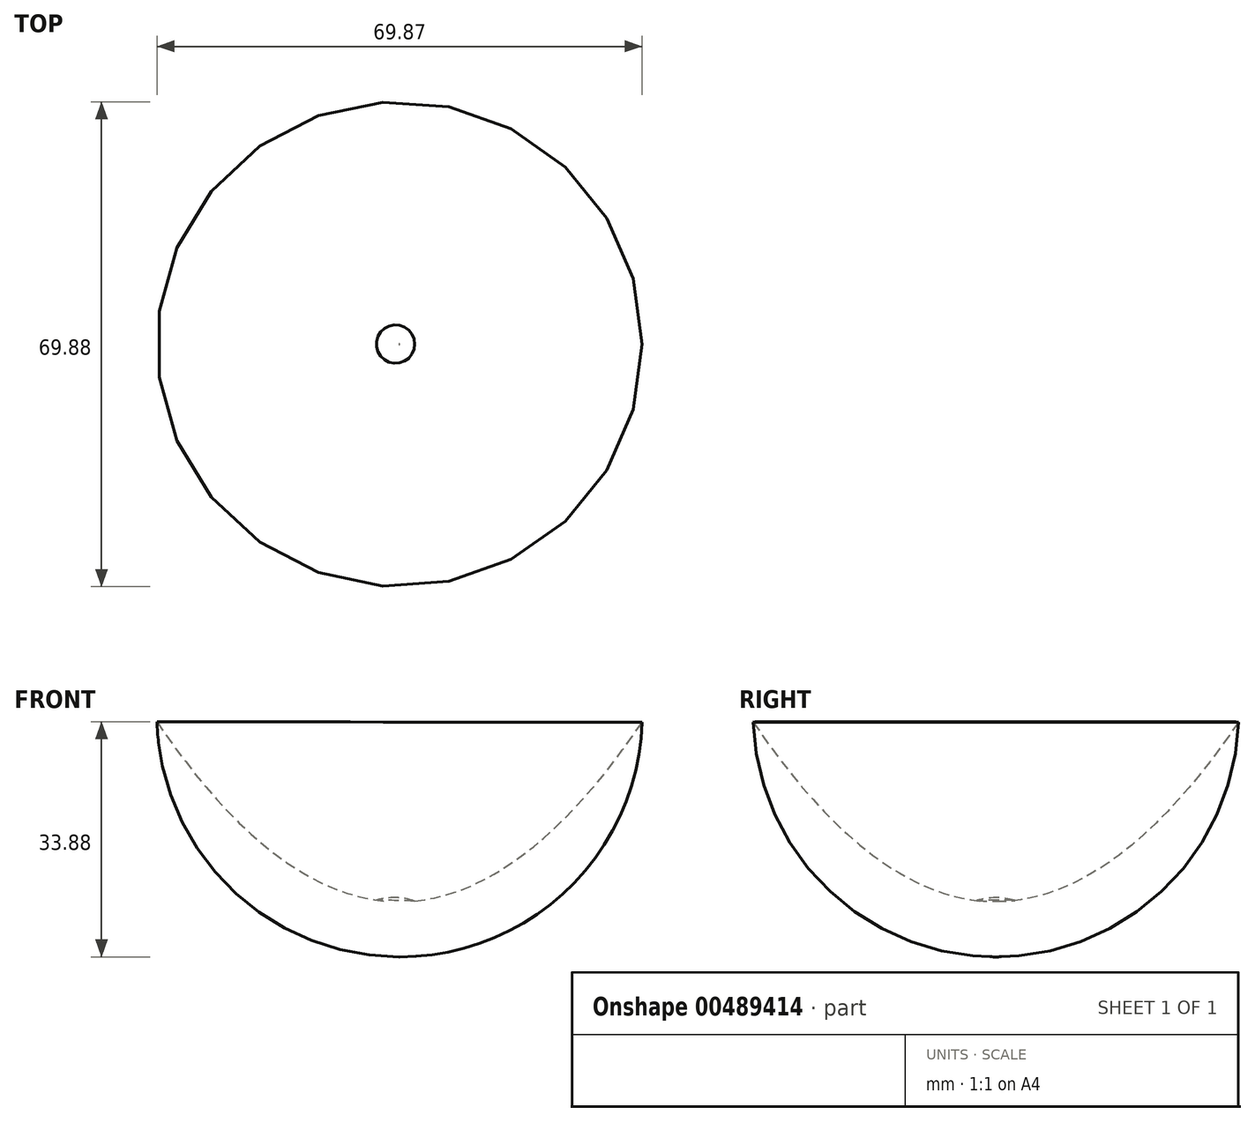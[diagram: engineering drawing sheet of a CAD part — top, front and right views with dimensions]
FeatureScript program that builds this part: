
annotation { "Feature Type Name" : "Feature", "Feature Type Description" : "" }
export const myFeature = defineFeature(function(context is Context, id is Id, definition is map)
    precondition{}
    {
        {
            var Q0;
            Q0=qCreatedBy(makeId("Front.planeOp"),FACE);
            var sketch = newSketch(context, id + "F0", { "sketchPlane" : qUnion([Q0])});
            skLineSegment(sketch, "E0", {"start": v(35.57, 70.99) * mm, "end": v(35.76, 70.99) * mm});
            skLineSegment(sketch, "E1", {"start": v(71.41, 35.92) * mm, "end": v(71.41, 35.79) * mm});
            skLineSegment(sketch, "E2", {"start": v(53.58, 0) * mm, "end": v(0, 0) * mm});
            skArc(sketch, "E3", {"start": v(70.67, 34.8) * mm, "mid": v(35.61, 70.84) * mm, "end": v(0.87, 34.5) * mm});
            skFitSpline(sketch, "E4", {"points": [v(-0.14, 35.5) * mm, v(35.7, 0) * mm, v(71.41, 35.92) * mm, v(70.69, 35.92) * mm], "startDerivative": vector(65.07, -127.42) * mm, "endDerivative": vector(-18.12, -6.85) * mm});
            skFitSpline(sketch, "E5", {"points": [v(56.44, 15.48) * mm, v(49.75, -23.32) * mm], "startDerivative": vector(-10.7, -38.8) * mm, "endDerivative": vector(-10.7, -38.8) * mm});
            skFitSpline(sketch, "E6.trimOffspring", {"points": [v(-0.14, 35.5) * mm, v(35.7, 0) * mm, v(71.41, 35.92) * mm, v(70.69, 35.92) * mm], "startDerivative": vector(65.07, -127.42) * mm, "endDerivative": vector(-18.12, -6.85) * mm});
            skLineSegment(sketch, "E7", {"start": v(35.76, 70.99) * mm, "end": v(35.7, 0) * mm});
            skPoint(sketch, "E7.startSnap0", {"position": v(35.57, 70.99) * mm});
            skFitSpline(sketch, "E8", {"points": [v(-0.14, 35.5) * mm, v(71.41, 35.92) * mm], "startDerivative": vector(71.86, -106.73) * mm, "endDerivative": vector(71.23, 107.5) * mm});
            skLineSegment(sketch, "E9", {"start": v(70.63, 33.99) * mm, "end": v(69.21, 32.6) * mm});
            skLineSegment(sketch, "E10", {"start": v(35.7, 0) * mm, "end": v(34.68, 1.01) * mm});
            skLineSegment(sketch, "E11", {"start": v(53.94, 17.75) * mm, "end": v(53.94, 17.75) * mm});
            skLineSegment(sketch, "E12.trimOffspring", {"start": v(0.87, 34.5) * mm, "end": v(-0.14, 35.5) * mm});
            skLineSegment(sketch, "E13.trimOffspring", {"start": v(36.74, 1) * mm, "end": v(35.7, 0) * mm});
            skArc(sketch, "E14.trimOffspring", {"start": v(0.9, 34) * mm, "mid": v(35.76, 1) * mm, "end": v(70.63, 33.99) * mm});
            skLineSegment(sketch, "E15", {"start": v(36.74, 1) * mm, "end": v(36.74, -75.7) * mm});
            skSolve(sketch);
        }
        {
            var Q0;
            {var subQ0=sQuery(id+"F0.wireOp",EDGE,"E3");var subQ2=sQuery(id+"F0.wireOp",EDGE,"E6.trimOffspring");var subQ7=makeQuery(id+"F0.imprint","INTERSECT",VERTEX,{"disambiguationData":[OD(1.0)],"derivedFrom":[subQ0,subQ2]});Q0=makeQuery(id+"F0.imprint","IMPRINT",FACE,{"disambiguationData":[TD([[makeQuery(id+"F0.imprint","IMPRINT",EDGE,{"disambiguationData":[TD([[subQ7,-1.0]])],"derivedFrom":subQ0}),1.0]])]});}
            var Q1;
            Q1=sQuery(id+"F0.wireOp",EDGE,"E7");
            revolve(context, id + "F1", {"entities" : qUnion([Q0]), "axis" : qUnion([Q1]), "revolveType" : RevolveType.FULL});
        }
        {
            var Q0;
            Q0=qCreatedBy(makeId("Top.planeOp"),FACE);
            var sketch = newSketch(context, id + "F2", { "sketchPlane" : qUnion([Q0])});
            skLineSegment(sketch, "E16", {"start": v(0, 0) * mm, "end": v(69.85, 0) * mm});
            skCircle(sketch, "E17", {"center": v(34.93, 0) * mm, "radius": 9.53 * mm});
            skSolve(sketch);
        }
        {
            var Q0;
            {var subQ0=sQuery(id+"F2.wireOp",EDGE,"E17");var subQ1=sQuery(id+"F2.wireOp",EDGE,"E16");var subQ2=makeQuery(id+"F2.imprint","INTERSECT",VERTEX,{"disambiguationData":[OD(0.0)],"derivedFrom":[subQ1,subQ0]});Q0=makeQuery(id+"F2.imprint","IMPRINT",FACE,{"disambiguationData":[TD([[makeQuery(id+"F2.imprint","IMPRINT",EDGE,{"disambiguationData":[TD([[subQ2,-1.0]])],"derivedFrom":subQ1}),1.0]])]});}
            var Q1;
            Q1=sQuery(id+"F2.wireOp",EDGE,"E16");
            revolve(context, id + "F3", {"operationType" : NewBodyOperationType.REMOVE, "entities" : qUnion([Q0]), "axis" : qUnion([Q1]), "revolveType" : RevolveType.FULL, "oppositeDirection" : true});
        }
    });
